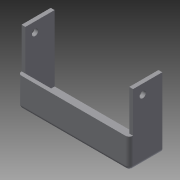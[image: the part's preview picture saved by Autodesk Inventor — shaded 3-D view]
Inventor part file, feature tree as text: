
AUTODESK INVENTOR PART (.ipt)
format: ipt  version: 2014 (Build 180170000, 170)  size: 119,808 bytes
history: native  units: in
note: dims shown in document units (in); Inventor stores cm internally (conversion verified against a paired STEP export)
features: extrude x3, sketch x3, fillet x1, hole x1
ambient origin geometry x8: Origin, YZ Plane, XZ Plane, XY Plane, X Axis, Y Axis, Z Axis, Center Point
bodies: Solid1 (feature_tree)
feature tree (8):
  extrude  "Extrusion1"  Depth=2.7in
  extrude  "Extrusion2"  TaperAngle=0.0deg  [1 undecoded]
  fillet  "Fillet1"  Radius=0.1in
  extrude  "Extrusion3"  Depth=0.1in
  hole  "Hole1"  [1 undecoded]
  sketch  "Sketch1"  dims[d0=0.67in d1=2.7in]
  sketch  "Sketch2"  dims[d2=0.1in d3=0.0in d4=0.0in d5=0.1in]
  sketch  "Sketch3"  dims[d6=0.1in d7=0.1in d8=0.86in d9=0.0in d10=0.1in d11=1.05in d12=0.0in d13=0.25in d14=0.25in d15=0.164in d16=0.75in d17=0.375in d18=0.25in d19=0.5635in d20=1.0in d21=0.8108in]
note: 2 required parameter values undecoded (feature->parameter linkage not recoverable at this tier; creation-order binding heuristic only, values carry confidence <= 0.55)
